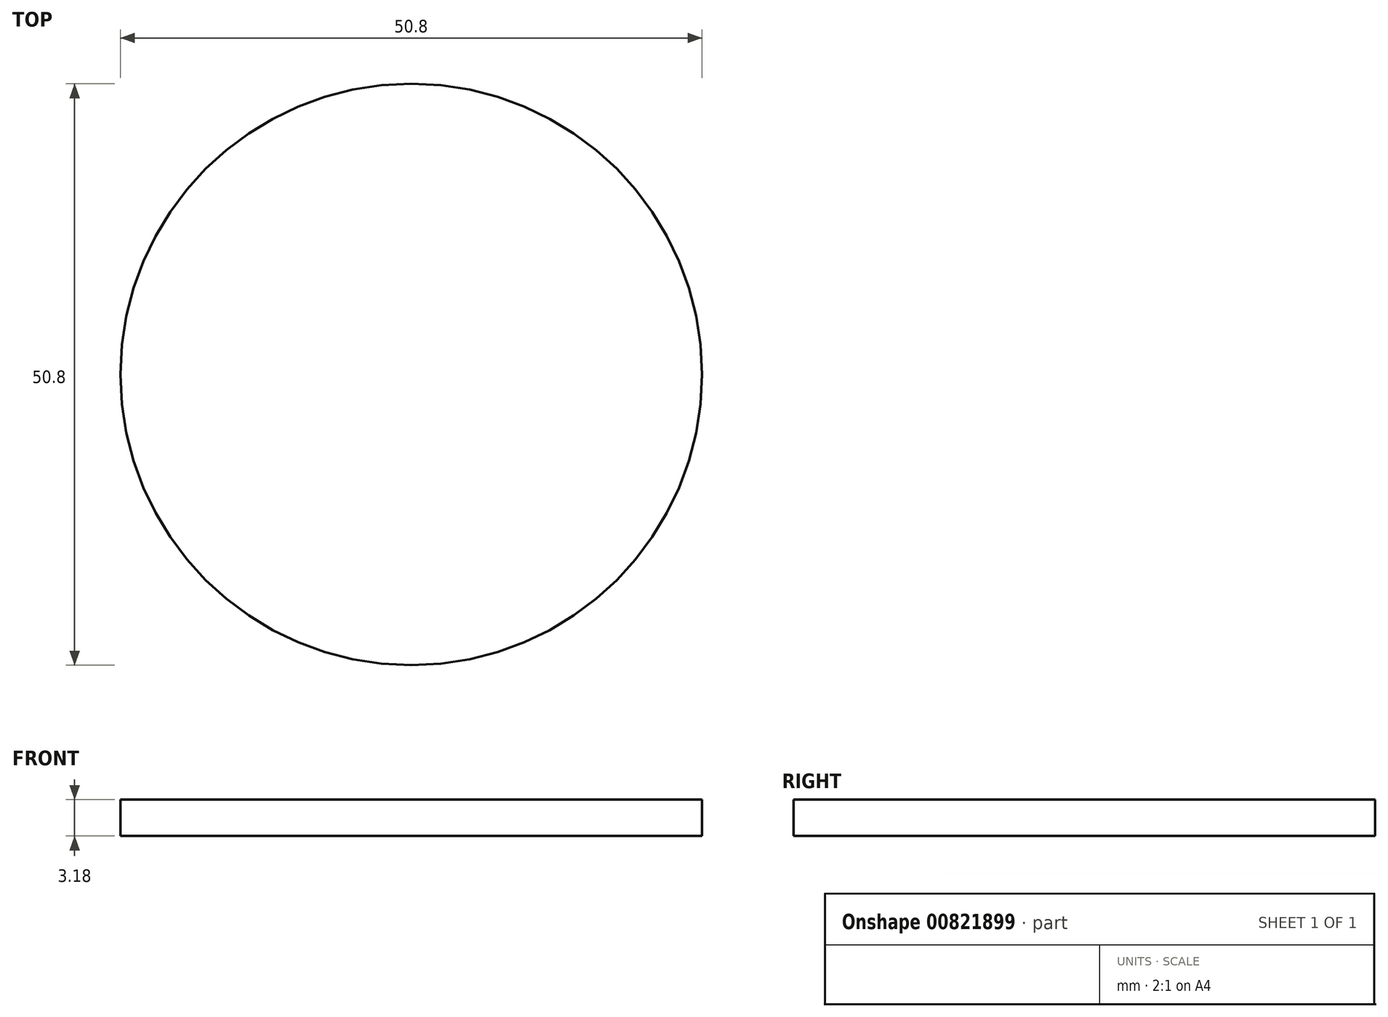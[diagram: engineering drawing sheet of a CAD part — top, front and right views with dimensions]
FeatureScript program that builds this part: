
annotation { "Feature Type Name" : "Feature", "Feature Type Description" : "" }
export const myFeature = defineFeature(function(context is Context, id is Id, definition is map)
    precondition{}
    {
        {
            var Q0;
            Q0=qCreatedBy(makeId("Top.planeOp"),FACE);
            var sketch = newSketch(context, id + "F0", { "sketchPlane" : qUnion([Q0])});
            skCircle(sketch, "E0", {"center": v(0, 0) * mm, "radius": 25.4 * mm});
            skSolve(sketch);
        }
        {
            var Q0;
            Q0=makeQuery(id+"F0.imprint","IMPRINT",FACE,{"disambiguationData":[TD([[makeQuery(id+"F0.imprint","IMPRINT",EDGE,{"derivedFrom":sQuery(id+"F0.wireOp",EDGE,"E0")}),1.0]])]});
            extrude(context, id + "F1", {"entities" : qUnion([Q0]), "depth" : 3.17 * mm, "offsetDistance" : 25.4 * mm});
        }
    });
